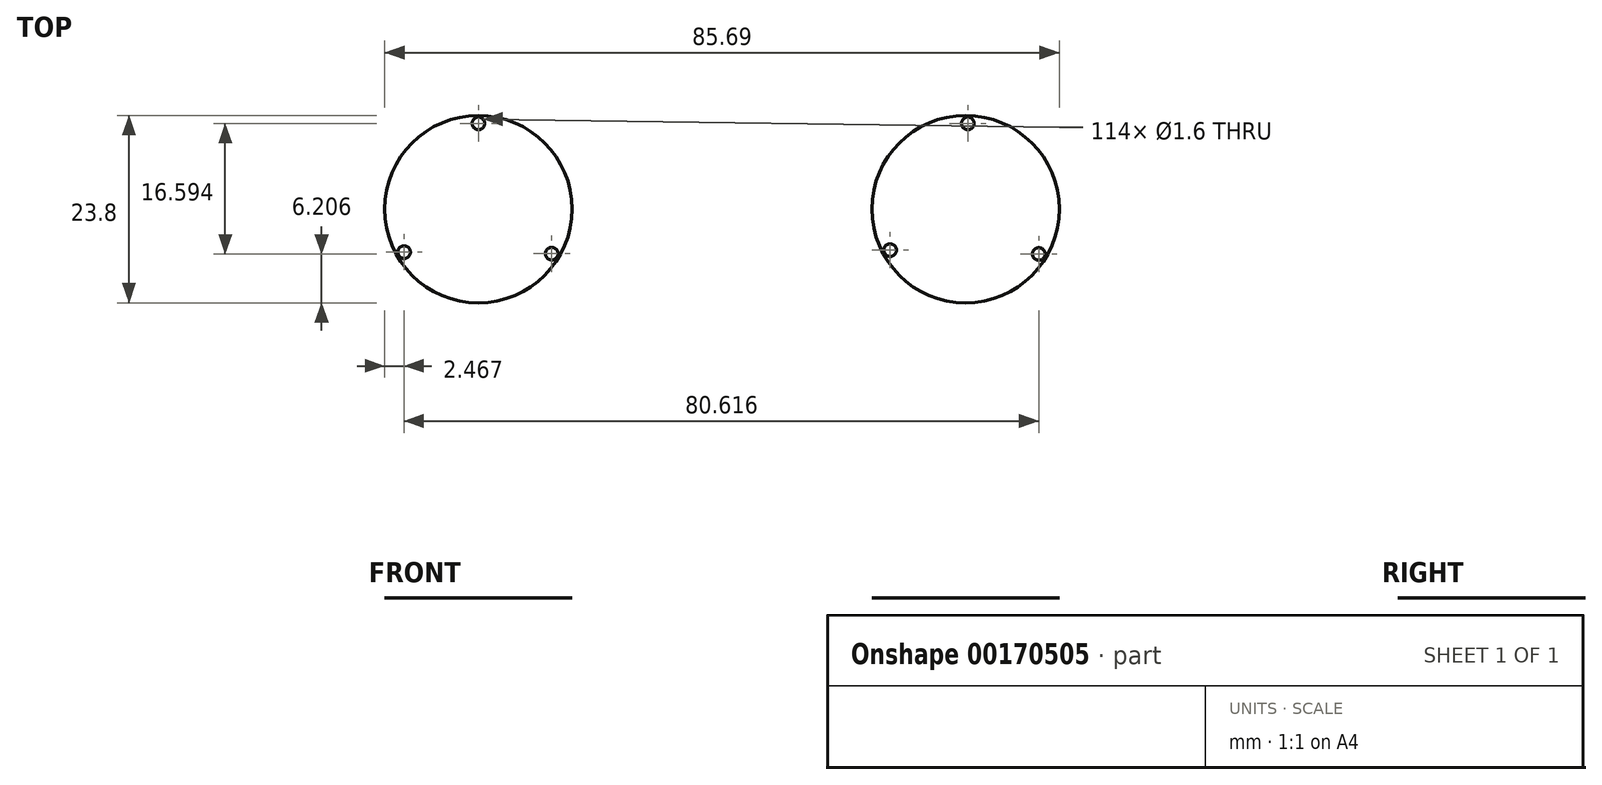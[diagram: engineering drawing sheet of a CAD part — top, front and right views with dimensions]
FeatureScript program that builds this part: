
annotation { "Feature Type Name" : "Feature", "Feature Type Description" : "" }
export const myFeature = defineFeature(function(context is Context, id is Id, definition is map)
    precondition{}
    {
        {
            var Q0;
            Q0=qCreatedBy(makeId("Top.planeOp"),FACE);
            var sketch = newSketch(context, id + "F0", { "sketchPlane" : qUnion([Q0])});
            skCircle(sketch, "E0", {"center": v(0, 0) * mm, "radius": 11.9 * mm});
            skCircle(sketch, "E1", {"center": v(0, 0) * mm, "radius": 10.9 * mm, "construction": true});
            skCircle(sketch, "E2", {"center": v(0, 10.9) * mm, "radius": 0.8 * mm});
            skCircle(sketch, "E3", {"center": v(9.32, -5.66) * mm, "radius": 0.8 * mm});
            skCircle(sketch, "E4", {"center": v(-9.43, -5.46) * mm, "radius": 0.8 * mm});
            skSolve(sketch);
        }
        {
            var Q0;
            {var subQ0=sQuery(id+"F0.wireOp",EDGE,"E2");Q0=makeQuery(id+"F0.imprint","IMPRINT",FACE,{"disambiguationData":[TD([[makeQuery(id+"F0.imprint","IMPRINT",EDGE,{"derivedFrom":subQ0}),-1.0]])]});}
            extrude(context, id + "F1", {"entities" : qUnion([Q0]), "depth" : 1 / 406.4 * mm});
        }
        {
            var Q0;
            Q0=qCreatedBy(makeId("Top.planeOp"),FACE);
            var sketch = newSketch(context, id + "F2", { "sketchPlane" : qUnion([Q0])});
            skCircle(sketch, "E5", {"center": v(61.89, 0) * mm, "radius": 11.9 * mm});
            skCircle(sketch, "E6", {"center": v(61.89, 0) * mm, "radius": 10.9 * mm, "construction": true});
            skCircle(sketch, "E7", {"center": v(62.17, 10.9) * mm, "radius": 0.8 * mm});
            skCircle(sketch, "E8.1.0", {"center": v(52.3, -5.2) * mm, "radius": 0.8 * mm});
            skCircle(sketch, "E8.2.0", {"center": v(71.18, -5.7) * mm, "radius": 0.8 * mm});
            skSolve(sketch);
        }
        {
            var Q0;
            Q0 = qSketchRegion(id + "F2", true);
            extrude(context, id + "F3", {"entities" : qUnion([Q0]), "depth" : 1 / 406.4 * mm});
        }
    });
